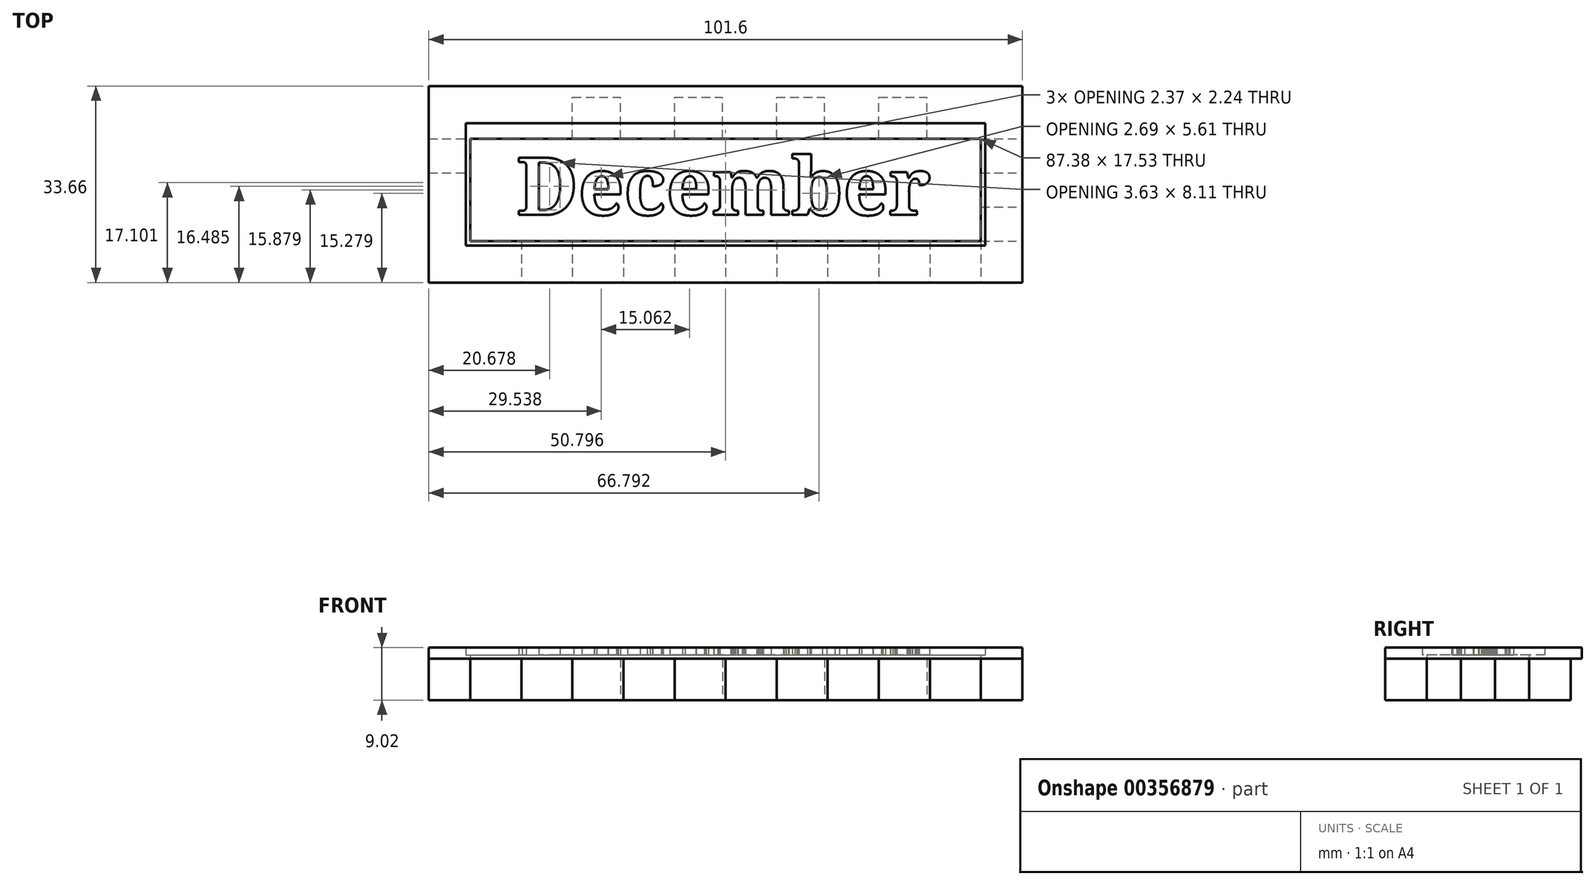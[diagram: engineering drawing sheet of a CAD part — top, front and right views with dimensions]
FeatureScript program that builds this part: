
annotation { "Feature Type Name" : "Feature", "Feature Type Description" : "" }
export const myFeature = defineFeature(function(context is Context, id is Id, definition is map)
    precondition{}
    {
        {
            var Q0;
            Q0=qCreatedBy(makeId("Top.planeOp"),FACE);
            var sketch = newSketch(context, id + "F0", { "sketchPlane" : qUnion([Q0])});
            skLineSegment(sketch, "E0.bottom", {"start": v(-52.12, 11.37) * mm, "end": v(49.48, 11.37) * mm});
            skLineSegment(sketch, "E0.top", {"start": v(-52.12, -20.38) * mm, "end": v(49.48, -20.38) * mm});
            skLineSegment(sketch, "E0.left", {"start": v(-52.12, 11.37) * mm, "end": v(-52.12, -20.38) * mm});
            skLineSegment(sketch, "E0.right", {"start": v(49.48, 11.37) * mm, "end": v(49.48, -20.38) * mm});
            skLineSegment(sketch, "E1.bottom", {"start": v(-52.12, 11.37) * mm, "end": v(-45.01, 11.37) * mm});
            skLineSegment(sketch, "E1.top", {"start": v(-52.12, 4.26) * mm, "end": v(-45.01, 4.26) * mm});
            skLineSegment(sketch, "E1.left", {"start": v(-52.12, 11.37) * mm, "end": v(-52.12, 4.26) * mm});
            skLineSegment(sketch, "E1.right", {"start": v(-45.01, 11.37) * mm, "end": v(-45.01, 4.26) * mm});
            skLineSegment(sketch, "E2.bottom", {"start": v(-45.01, 11.37) * mm, "end": v(-36.78, 11.37) * mm});
            skLineSegment(sketch, "E2.top", {"start": v(-45.01, 4.26) * mm, "end": v(-36.78, 4.26) * mm});
            skLineSegment(sketch, "E2.right", {"start": v(-36.78, 11.37) * mm, "end": v(-36.78, 4.26) * mm});
            skLineSegment(sketch, "E3.bottom", {"start": v(-36.78, 4.26) * mm, "end": v(-27.54, 4.26) * mm});
            skLineSegment(sketch, "E3.top", {"start": v(-36.78, 11.37) * mm, "end": v(-27.54, 11.37) * mm});
            skLineSegment(sketch, "E3.left", {"start": v(-36.78, 4.26) * mm, "end": v(-36.78, 11.37) * mm});
            skLineSegment(sketch, "E3.right", {"start": v(-27.54, 4.26) * mm, "end": v(-27.54, 11.37) * mm});
            skLineSegment(sketch, "E4.bottom", {"start": v(-27.54, 4.26) * mm, "end": v(-19.3, 4.26) * mm});
            skLineSegment(sketch, "E4.top", {"start": v(-27.54, 11.37) * mm, "end": v(-19.3, 11.37) * mm});
            skLineSegment(sketch, "E4.right", {"start": v(-19.3, 4.26) * mm, "end": v(-19.3, 11.37) * mm});
            skLineSegment(sketch, "E5.bottom", {"start": v(-19.3, 4.26) * mm, "end": v(-10.06, 4.26) * mm});
            skLineSegment(sketch, "E5.top", {"start": v(-19.3, 11.37) * mm, "end": v(-10.06, 11.37) * mm});
            skLineSegment(sketch, "E5.right", {"start": v(-10.06, 4.26) * mm, "end": v(-10.06, 11.37) * mm});
            skLineSegment(sketch, "E6.bottom", {"start": v(-10.06, 4.26) * mm, "end": v(-10.06, 4.26) * mm});
            skLineSegment(sketch, "E6.top", {"start": v(-10.06, 11.37) * mm, "end": v(-10.06, 11.37) * mm});
            skLineSegment(sketch, "E7.bottom", {"start": v(-10.06, 4.26) * mm, "end": v(-1.83, 4.26) * mm});
            skLineSegment(sketch, "E7.top", {"start": v(-10.06, 11.37) * mm, "end": v(-1.83, 11.37) * mm});
            skLineSegment(sketch, "E7.right", {"start": v(-1.83, 4.26) * mm, "end": v(-1.83, 11.37) * mm});
            skLineSegment(sketch, "E8.bottom", {"start": v(-1.83, 4.26) * mm, "end": v(7.41, 4.26) * mm});
            skLineSegment(sketch, "E8.top", {"start": v(-1.83, 11.37) * mm, "end": v(7.41, 11.37) * mm});
            skLineSegment(sketch, "E8.right", {"start": v(7.41, 4.26) * mm, "end": v(7.41, 11.37) * mm});
            skLineSegment(sketch, "E9.bottom", {"start": v(7.41, 4.26) * mm, "end": v(15.64, 4.26) * mm});
            skLineSegment(sketch, "E9.top", {"start": v(7.41, 11.37) * mm, "end": v(15.64, 11.37) * mm});
            skLineSegment(sketch, "E9.right", {"start": v(15.64, 4.26) * mm, "end": v(15.64, 11.37) * mm});
            skLineSegment(sketch, "E10.bottom", {"start": v(15.64, 4.26) * mm, "end": v(24.89, 4.26) * mm});
            skLineSegment(sketch, "E10.top", {"start": v(15.64, 11.37) * mm, "end": v(24.89, 11.37) * mm});
            skLineSegment(sketch, "E10.right", {"start": v(24.89, 4.26) * mm, "end": v(24.89, 11.37) * mm});
            skLineSegment(sketch, "E11.bottom", {"start": v(24.89, 4.26) * mm, "end": v(24.89, 4.26) * mm});
            skLineSegment(sketch, "E11.top", {"start": v(24.89, 11.37) * mm, "end": v(24.89, 11.37) * mm});
            skLineSegment(sketch, "E12.bottom", {"start": v(24.89, 4.26) * mm, "end": v(33.12, 4.26) * mm});
            skLineSegment(sketch, "E12.top", {"start": v(24.89, 11.37) * mm, "end": v(33.12, 11.37) * mm});
            skLineSegment(sketch, "E12.right", {"start": v(33.12, 4.26) * mm, "end": v(33.12, 11.37) * mm});
            skLineSegment(sketch, "E13.bottom", {"start": v(33.12, 4.26) * mm, "end": v(42.36, 4.26) * mm});
            skLineSegment(sketch, "E13.top", {"start": v(33.12, 11.37) * mm, "end": v(42.36, 11.37) * mm});
            skLineSegment(sketch, "E13.right", {"start": v(42.36, 4.26) * mm, "end": v(42.36, 11.37) * mm});
            skLineSegment(sketch, "E14.bottom", {"start": v(42.36, 4.26) * mm, "end": v(49.48, 4.26) * mm});
            skLineSegment(sketch, "E14.top", {"start": v(42.36, 11.37) * mm, "end": v(49.48, 11.37) * mm});
            skLineSegment(sketch, "E14.right", {"start": v(49.48, 4.26) * mm, "end": v(49.48, 11.37) * mm});
            skLineSegment(sketch, "E15.bottom", {"start": v(-52.12, -20.38) * mm, "end": v(-45.01, -20.38) * mm});
            skLineSegment(sketch, "E15.top", {"start": v(-52.12, -13.26) * mm, "end": v(-45.01, -13.26) * mm});
            skLineSegment(sketch, "E15.left", {"start": v(-52.12, -20.38) * mm, "end": v(-52.12, -13.26) * mm});
            skLineSegment(sketch, "E15.right", {"start": v(-45.01, -20.38) * mm, "end": v(-45.01, -13.26) * mm});
            skLineSegment(sketch, "E16.bottom", {"start": v(-45.01, -13.26) * mm, "end": v(-45.01, -13.26) * mm});
            skLineSegment(sketch, "E16.top", {"start": v(-45.01, -20.38) * mm, "end": v(-45.01, -20.38) * mm});
            skLineSegment(sketch, "E16.left", {"start": v(-45.01, -13.26) * mm, "end": v(-45.01, -20.38) * mm});
            skLineSegment(sketch, "E16.right", {"start": v(-45.01, -13.26) * mm, "end": v(-45.01, -20.38) * mm});
            skLineSegment(sketch, "E17.bottom", {"start": v(-45.01, -13.26) * mm, "end": v(-36.27, -13.26) * mm});
            skLineSegment(sketch, "E17.top", {"start": v(-45.01, -20.38) * mm, "end": v(-36.27, -20.38) * mm});
            skLineSegment(sketch, "E17.right", {"start": v(-36.27, -13.26) * mm, "end": v(-36.27, -20.38) * mm});
            skLineSegment(sketch, "E18.bottom", {"start": v(-36.27, -13.26) * mm, "end": v(-36.27, -13.26) * mm});
            skLineSegment(sketch, "E18.top", {"start": v(-36.27, -20.38) * mm, "end": v(-36.27, -20.38) * mm});
            skLineSegment(sketch, "E19.bottom", {"start": v(-36.27, -13.26) * mm, "end": v(-27.54, -13.26) * mm});
            skLineSegment(sketch, "E19.top", {"start": v(-36.27, -20.38) * mm, "end": v(-27.54, -20.38) * mm});
            skLineSegment(sketch, "E19.right", {"start": v(-27.54, -13.26) * mm, "end": v(-27.54, -20.38) * mm});
            skLineSegment(sketch, "E20.bottom", {"start": v(-27.54, -13.26) * mm, "end": v(-18.8, -13.26) * mm});
            skLineSegment(sketch, "E20.top", {"start": v(-27.54, -20.38) * mm, "end": v(-18.8, -20.38) * mm});
            skLineSegment(sketch, "E20.right", {"start": v(-18.8, -13.26) * mm, "end": v(-18.8, -20.38) * mm});
            skLineSegment(sketch, "E21.bottom", {"start": v(-18.8, -13.26) * mm, "end": v(-10.06, -13.26) * mm});
            skLineSegment(sketch, "E21.top", {"start": v(-18.8, -20.38) * mm, "end": v(-10.06, -20.38) * mm});
            skLineSegment(sketch, "E21.right", {"start": v(-10.06, -13.26) * mm, "end": v(-10.06, -20.38) * mm});
            skLineSegment(sketch, "E22.bottom", {"start": v(-10.06, -13.26) * mm, "end": v(-1.32, -13.26) * mm});
            skLineSegment(sketch, "E22.top", {"start": v(-10.06, -20.38) * mm, "end": v(-1.32, -20.38) * mm});
            skLineSegment(sketch, "E22.right", {"start": v(-1.32, -13.26) * mm, "end": v(-1.32, -20.38) * mm});
            skLineSegment(sketch, "E23.bottom", {"start": v(-1.32, -13.26) * mm, "end": v(7.41, -13.26) * mm});
            skLineSegment(sketch, "E23.top", {"start": v(-1.32, -20.38) * mm, "end": v(7.41, -20.38) * mm});
            skLineSegment(sketch, "E23.right", {"start": v(7.41, -13.26) * mm, "end": v(7.41, -20.38) * mm});
            skLineSegment(sketch, "E24.bottom", {"start": v(7.41, -13.26) * mm, "end": v(16.15, -13.26) * mm});
            skLineSegment(sketch, "E24.top", {"start": v(7.41, -20.38) * mm, "end": v(16.15, -20.38) * mm});
            skLineSegment(sketch, "E24.right", {"start": v(16.15, -13.26) * mm, "end": v(16.15, -20.38) * mm});
            skLineSegment(sketch, "E25.bottom", {"start": v(16.15, -13.26) * mm, "end": v(24.89, -13.26) * mm});
            skLineSegment(sketch, "E25.top", {"start": v(16.15, -20.38) * mm, "end": v(24.89, -20.38) * mm});
            skLineSegment(sketch, "E25.right", {"start": v(24.89, -13.26) * mm, "end": v(24.89, -20.38) * mm});
            skLineSegment(sketch, "E26.bottom", {"start": v(24.89, -13.26) * mm, "end": v(33.63, -13.26) * mm});
            skLineSegment(sketch, "E26.top", {"start": v(24.89, -20.38) * mm, "end": v(33.63, -20.38) * mm});
            skLineSegment(sketch, "E26.right", {"start": v(33.63, -13.26) * mm, "end": v(33.63, -20.38) * mm});
            skLineSegment(sketch, "E27.bottom", {"start": v(33.63, -13.26) * mm, "end": v(42.36, -13.26) * mm});
            skLineSegment(sketch, "E27.top", {"start": v(33.63, -20.38) * mm, "end": v(42.36, -20.38) * mm});
            skLineSegment(sketch, "E27.right", {"start": v(42.36, -13.26) * mm, "end": v(42.36, -20.38) * mm});
            skLineSegment(sketch, "E28.bottom", {"start": v(42.36, -13.26) * mm, "end": v(49.48, -13.26) * mm});
            skLineSegment(sketch, "E28.top", {"start": v(42.36, -20.38) * mm, "end": v(49.48, -20.38) * mm});
            skLineSegment(sketch, "E28.right", {"start": v(49.48, -13.26) * mm, "end": v(49.48, -20.38) * mm});
            skLineSegment(sketch, "E29.top", {"start": v(-52.12, -1.58) * mm, "end": v(-45.01, -1.58) * mm});
            skLineSegment(sketch, "E29.left", {"start": v(-52.12, 4.26) * mm, "end": v(-52.12, -1.58) * mm});
            skLineSegment(sketch, "E29.right", {"start": v(-45.01, 4.26) * mm, "end": v(-45.01, -1.58) * mm});
            skLineSegment(sketch, "E30.top", {"start": v(-52.12, -7.42) * mm, "end": v(-45.01, -7.42) * mm});
            skLineSegment(sketch, "E30.left", {"start": v(-52.12, -1.58) * mm, "end": v(-52.12, -7.42) * mm});
            skLineSegment(sketch, "E30.right", {"start": v(-45.01, -1.58) * mm, "end": v(-45.01, -7.42) * mm});
            skLineSegment(sketch, "E31.bottom", {"start": v(-45.01, -7.42) * mm, "end": v(-52.12, -7.42) * mm});
            skLineSegment(sketch, "E31.top", {"start": v(-45.01, -13.26) * mm, "end": v(-52.12, -13.26) * mm});
            skLineSegment(sketch, "E31.left", {"start": v(-45.01, -7.42) * mm, "end": v(-45.01, -13.26) * mm});
            skLineSegment(sketch, "E31.right", {"start": v(-52.12, -7.42) * mm, "end": v(-52.12, -13.26) * mm});
            skLineSegment(sketch, "E32.top", {"start": v(42.36, -1.58) * mm, "end": v(49.48, -1.58) * mm});
            skLineSegment(sketch, "E32.left", {"start": v(42.36, 4.26) * mm, "end": v(42.36, -1.58) * mm});
            skLineSegment(sketch, "E32.right", {"start": v(49.48, 4.26) * mm, "end": v(49.48, -1.58) * mm});
            skLineSegment(sketch, "E33.top", {"start": v(42.36, -7.42) * mm, "end": v(49.48, -7.42) * mm});
            skLineSegment(sketch, "E33.left", {"start": v(42.36, -1.58) * mm, "end": v(42.36, -7.42) * mm});
            skLineSegment(sketch, "E33.right", {"start": v(49.48, -1.58) * mm, "end": v(49.48, -7.42) * mm});
            skLineSegment(sketch, "E34.left", {"start": v(42.36, -7.42) * mm, "end": v(42.36, -13.26) * mm});
            skLineSegment(sketch, "E34.right", {"start": v(49.48, -7.42) * mm, "end": v(49.48, -13.26) * mm});
            skSolve(sketch);
        }
        {
            var Q0;
            Q0=makeQuery(id+"F0.imprint","IMPRINT",FACE,{"disambiguationData":[TD([[makeQuery(id+"F0.imprint","IMPRINT",EDGE,{"derivedFrom":sQuery(id+"F0.wireOp",EDGE,"E2.top")}),-1.0]])]});
            var Q1;
            Q1=makeQuery(id+"F0.imprint","IMPRINT",FACE,{"disambiguationData":[TD([[makeQuery(id+"F0.imprint","IMPRINT",EDGE,{"derivedFrom":sQuery(id+"F0.wireOp",EDGE,"E2.bottom")}),-1.0]])]});
            var Q2;
            Q2=makeQuery(id+"F0.imprint","IMPRINT",FACE,{"disambiguationData":[TD([[makeQuery(id+"F0.imprint","IMPRINT",EDGE,{"derivedFrom":sQuery(id+"F0.wireOp",EDGE,"E4.bottom")}),1.0]])]});
            var Q3;
            Q3=makeQuery(id+"F0.imprint","IMPRINT",FACE,{"disambiguationData":[TD([[makeQuery(id+"F0.imprint","IMPRINT",EDGE,{"derivedFrom":sQuery(id+"F0.wireOp",EDGE,"E7.bottom")}),1.0]])]});
            var Q4;
            Q4=makeQuery(id+"F0.imprint","IMPRINT",FACE,{"disambiguationData":[TD([[makeQuery(id+"F0.imprint","IMPRINT",EDGE,{"derivedFrom":sQuery(id+"F0.wireOp",EDGE,"E9.bottom")}),1.0]])]});
            var Q5;
            Q5=makeQuery(id+"F0.imprint","IMPRINT",FACE,{"disambiguationData":[TD([[makeQuery(id+"F0.imprint","IMPRINT",EDGE,{"derivedFrom":sQuery(id+"F0.wireOp",EDGE,"E12.bottom")}),1.0]])]});
            var Q6;
            Q6=makeQuery(id+"F0.imprint","IMPRINT",FACE,{"disambiguationData":[TD([[makeQuery(id+"F0.imprint","IMPRINT",EDGE,{"derivedFrom":sQuery(id+"F0.wireOp",EDGE,"E14.bottom")}),-1.0]])]});
            var Q7;
            Q7=makeQuery(id+"F0.imprint","IMPRINT",FACE,{"disambiguationData":[TD([[makeQuery(id+"F0.imprint","IMPRINT",EDGE,{"derivedFrom":sQuery(id+"F0.wireOp",EDGE,"E33.top")}),-1.0]])]});
            var Q8;
            Q8=makeQuery(id+"F0.imprint","IMPRINT",FACE,{"disambiguationData":[TD([[makeQuery(id+"F0.imprint","IMPRINT",EDGE,{"derivedFrom":sQuery(id+"F0.wireOp",EDGE,"E27.bottom")}),-1.0]])]});
            var Q9;
            Q9=makeQuery(id+"F0.imprint","IMPRINT",FACE,{"disambiguationData":[TD([[makeQuery(id+"F0.imprint","IMPRINT",EDGE,{"derivedFrom":sQuery(id+"F0.wireOp",EDGE,"E25.bottom")}),-1.0]])]});
            var Q10;
            Q10=makeQuery(id+"F0.imprint","IMPRINT",FACE,{"disambiguationData":[TD([[makeQuery(id+"F0.imprint","IMPRINT",EDGE,{"derivedFrom":sQuery(id+"F0.wireOp",EDGE,"E23.bottom")}),-1.0]])]});
            var Q11;
            Q11=makeQuery(id+"F0.imprint","IMPRINT",FACE,{"disambiguationData":[TD([[makeQuery(id+"F0.imprint","IMPRINT",EDGE,{"derivedFrom":sQuery(id+"F0.wireOp",EDGE,"E21.bottom")}),-1.0]])]});
            var Q12;
            Q12=makeQuery(id+"F0.imprint","IMPRINT",FACE,{"disambiguationData":[TD([[makeQuery(id+"F0.imprint","IMPRINT",EDGE,{"derivedFrom":sQuery(id+"F0.wireOp",EDGE,"E19.bottom")}),-1.0]])]});
            var Q13;
            Q13=makeQuery(id+"F0.imprint","IMPRINT",FACE,{"disambiguationData":[TD([[makeQuery(id+"F0.imprint","IMPRINT",EDGE,{"derivedFrom":sQuery(id+"F0.wireOp",EDGE,"E31.bottom")}),1.0]])]});
            var Q14;
            Q14=makeQuery(id+"F0.imprint","IMPRINT",FACE,{"disambiguationData":[TD([[makeQuery(id+"F0.imprint","IMPRINT",EDGE,{"derivedFrom":sQuery(id+"F0.wireOp",EDGE,"E1.top")}),-1.0]])]});
            extrude(context, id + "F1", {"entities" : qUnion([Q0, Q1, Q2, Q3, Q4, Q5, Q6, Q7, Q8, Q9, Q10, Q11, Q12, Q13, Q14]), "depth" : 7.11 * mm});
        }
        {
            var Q0;
            Q0=makeQuery(id+"F1.opExtrude","CAP_FACE",FACE,{"disambiguationData":[OSD([sQuery(id+"F0.wireOp",EDGE,"E2.bottom"),sQuery(id+"F0.wireOp",EDGE,"E1.right"),sQuery(id+"F0.wireOp",EDGE,"E3.bottom"),sQuery(id+"F0.wireOp",EDGE,"E3.left"),sQuery(id+"F0.wireOp",EDGE,"E4.top"),sQuery(id+"F0.wireOp",EDGE,"E3.right"),sQuery(id+"F0.wireOp",EDGE,"E5.bottom"),sQuery(id+"F0.wireOp",EDGE,"E4.right"),sQuery(id+"F0.wireOp",EDGE,"E6.top"),sQuery(id+"F0.wireOp",EDGE,"E5.right"),sQuery(id+"F0.wireOp",EDGE,"E7.bottom"),sQuery(id+"F0.wireOp",EDGE,"E5.right"),sQuery(id+"F0.wireOp",EDGE,"E8.top"),sQuery(id+"F0.wireOp",EDGE,"E7.right"),sQuery(id+"F0.wireOp",EDGE,"E9.bottom"),sQuery(id+"F0.wireOp",EDGE,"E8.right"),sQuery(id+"F0.wireOp",EDGE,"E10.top"),sQuery(id+"F0.wireOp",EDGE,"E9.right"),sQuery(id+"F0.wireOp",EDGE,"E11.bottom"),sQuery(id+"F0.wireOp",EDGE,"E10.right"),sQuery(id+"F0.wireOp",EDGE,"E12.top"),sQuery(id+"F0.wireOp",EDGE,"E10.right"),sQuery(id+"F0.wireOp",EDGE,"E13.bottom"),sQuery(id+"F0.wireOp",EDGE,"E12.right"),sQuery(id+"F0.wireOp",EDGE,"E16.bottom"),sQuery(id+"F0.wireOp",EDGE,"E17.top"),sQuery(id+"F0.wireOp",EDGE,"E16.left"),sQuery(id+"F0.wireOp",EDGE,"E18.bottom"),sQuery(id+"F0.wireOp",EDGE,"E17.right"),sQuery(id+"F0.wireOp",EDGE,"E19.top"),sQuery(id+"F0.wireOp",EDGE,"E17.right"),sQuery(id+"F0.wireOp",EDGE,"E20.bottom"),sQuery(id+"F0.wireOp",EDGE,"E19.right"),sQuery(id+"F0.wireOp",EDGE,"E21.top"),sQuery(id+"F0.wireOp",EDGE,"E20.right"),sQuery(id+"F0.wireOp",EDGE,"E22.bottom"),sQuery(id+"F0.wireOp",EDGE,"E21.right"),sQuery(id+"F0.wireOp",EDGE,"E23.top"),sQuery(id+"F0.wireOp",EDGE,"E22.right"),sQuery(id+"F0.wireOp",EDGE,"E24.bottom"),sQuery(id+"F0.wireOp",EDGE,"E23.right"),sQuery(id+"F0.wireOp",EDGE,"E25.top"),sQuery(id+"F0.wireOp",EDGE,"E24.right"),sQuery(id+"F0.wireOp",EDGE,"E26.bottom"),sQuery(id+"F0.wireOp",EDGE,"E25.right"),sQuery(id+"F0.wireOp",EDGE,"E27.top"),sQuery(id+"F0.wireOp",EDGE,"E26.right"),sQuery(id+"F0.wireOp",EDGE,"E27.right"),sQuery(id+"F0.wireOp",EDGE,"E1.top"),sQuery(id+"F0.wireOp",EDGE,"E29.left"),sQuery(id+"F0.wireOp",EDGE,"E29.top"),sQuery(id+"F0.wireOp",EDGE,"E30.right"),sQuery(id+"F0.wireOp",EDGE,"E31.bottom"),sQuery(id+"F0.wireOp",EDGE,"E31.top"),sQuery(id+"F0.wireOp",EDGE,"E31.right"),sQuery(id+"F0.wireOp",EDGE,"E14.bottom"),sQuery(id+"F0.wireOp",EDGE,"E32.right"),sQuery(id+"F0.wireOp",EDGE,"E32.top"),sQuery(id+"F0.wireOp",EDGE,"E33.left"),sQuery(id+"F0.wireOp",EDGE,"E33.top"),sQuery(id+"F0.wireOp",EDGE,"E28.bottom"),sQuery(id+"F0.wireOp",EDGE,"E34.right")])],"isStart":false});
            var sketch = newSketch(context, id + "F2", { "sketchPlane" : qUnion([Q0])});
            skLineSegment(sketch, "E35.bottom", {"start": v(-52.12, -20.38) * mm, "end": v(-45.01, -20.38) * mm});
            skLineSegment(sketch, "E35.top", {"start": v(-52.12, 13.28) * mm, "end": v(-45.01, 13.28) * mm});
            skLineSegment(sketch, "E35.left", {"start": v(-52.12, -20.38) * mm, "end": v(-52.12, 13.28) * mm});
            skLineSegment(sketch, "E35.right", {"start": v(-45.01, -20.38) * mm, "end": v(-45.01, 13.28) * mm});
            skLineSegment(sketch, "E36.bottom", {"start": v(-52.12, -20.38) * mm, "end": v(49.48, -20.38) * mm});
            skLineSegment(sketch, "E36.top", {"start": v(-52.12, -13.26) * mm, "end": v(49.48, -13.26) * mm});
            skLineSegment(sketch, "E36.left", {"start": v(-52.12, -20.38) * mm, "end": v(-52.12, -13.26) * mm});
            skLineSegment(sketch, "E36.right", {"start": v(49.48, -20.38) * mm, "end": v(49.48, -13.26) * mm});
            skPoint(sketch, "E37.oppositeSnap0", {"position": v(42.36, -4.5) * mm});
            skLineSegment(sketch, "E37.bottom", {"start": v(49.48, -20.38) * mm, "end": v(42.36, -20.38) * mm});
            skLineSegment(sketch, "E37.top", {"start": v(49.48, 13.28) * mm, "end": v(42.36, 13.28) * mm});
            skLineSegment(sketch, "E37.left", {"start": v(49.48, -20.38) * mm, "end": v(49.48, 13.28) * mm});
            skLineSegment(sketch, "E37.right", {"start": v(42.36, -20.38) * mm, "end": v(42.36, 13.28) * mm});
            skLineSegment(sketch, "E38.bottom", {"start": v(-52.12, 13.28) * mm, "end": v(49.48, 13.28) * mm});
            skLineSegment(sketch, "E38.top", {"start": v(-52.12, 4.26) * mm, "end": v(49.48, 4.26) * mm});
            skLineSegment(sketch, "E38.left", {"start": v(-52.12, 13.28) * mm, "end": v(-52.12, 4.26) * mm});
            skLineSegment(sketch, "E38.right", {"start": v(49.48, 13.28) * mm, "end": v(49.48, 4.26) * mm});
            skSolve(sketch);
        }
        {
            var Q0;
            Q0=qSketchRegion(id+"F2",true);
            var Q1;
            {var subQ5=sQuery(id+"F2.wireOp",EDGE,"E36.top");var subQ10=sQuery(id+"F2.wireOp",EDGE,"E35.right");var subQ12=makeQuery(id+"F2.imprint","INTERSECT",VERTEX,{"derivedFrom":[makeQuery(id+"F1.opExtrude","CAP_EDGE",EDGE,{"disambiguationData":[OSD([sQuery(id+"F0.wireOp",EDGE,"E31.bottom")])],"isStart":false}),subQ10]});var subQ24=makeQuery(id+"F2.imprint","INTERSECT",VERTEX,{"derivedFrom":[subQ10,subQ5]});Q1=makeQuery(id+"F2.imprint","IMPRINT",FACE,{"disambiguationData":[TD([[makeQuery(id+"F2.imprint","IMPRINT",EDGE,{"disambiguationData":[TD([[subQ12,1.0],[subQ24,-1.0]])],"derivedFrom":subQ10}),-1.0]])]});}
            extrude(context, id + "F3", {"entities" : qUnion([Q0, Q1]), "depth" : 0.64 * mm});
        }
        {
            var Q0;
            Q0=makeQuery(id+"F3.opExtrude","CAP_FACE",FACE,{"disambiguationData":[OSD([sQuery(id+"F2.wireOp",EDGE,"E35.left"),sQuery(id+"F2.wireOp",EDGE,"E36.bottom"),sQuery(id+"F2.wireOp",EDGE,"E36.left"),sQuery(id+"F2.wireOp",EDGE,"E37.bottom"),sQuery(id+"F2.wireOp",EDGE,"E37.left"),sQuery(id+"F2.wireOp",EDGE,"E38.bottom"),sQuery(id+"F2.wireOp",EDGE,"E38.left"),sQuery(id+"F2.wireOp",EDGE,"E38.right")])],"isStart":false});
            var sketch = newSketch(context, id + "F4", { "sketchPlane" : qUnion([Q0])});
            skLineSegment(sketch, "E39.bottom", {"start": v(-52.12, 13.28) * mm, "end": v(49.48, 13.28) * mm});
            skLineSegment(sketch, "E39.top", {"start": v(-52.12, 6.93) * mm, "end": v(49.48, 6.93) * mm});
            skLineSegment(sketch, "E39.left", {"start": v(-52.12, 13.28) * mm, "end": v(-52.12, 6.93) * mm});
            skLineSegment(sketch, "E39.right", {"start": v(49.48, 13.28) * mm, "end": v(49.48, 6.93) * mm});
            skLineSegment(sketch, "E40.bottom", {"start": v(-52.12, 13.28) * mm, "end": v(-45.77, 13.28) * mm});
            skLineSegment(sketch, "E40.top", {"start": v(-52.12, -20.38) * mm, "end": v(-45.77, -20.38) * mm});
            skLineSegment(sketch, "E40.left", {"start": v(-52.12, 13.28) * mm, "end": v(-52.12, -20.38) * mm});
            skLineSegment(sketch, "E40.right", {"start": v(-45.77, 13.28) * mm, "end": v(-45.77, -20.38) * mm});
            skLineSegment(sketch, "E41.bottom", {"start": v(-52.12, -14.03) * mm, "end": v(49.48, -14.03) * mm});
            skLineSegment(sketch, "E41.top", {"start": v(-52.12, -20.38) * mm, "end": v(49.48, -20.38) * mm});
            skLineSegment(sketch, "E41.left", {"start": v(-52.12, -14.03) * mm, "end": v(-52.12, -20.38) * mm});
            skLineSegment(sketch, "E41.right", {"start": v(49.48, -14.03) * mm, "end": v(49.48, -20.38) * mm});
            skLineSegment(sketch, "E42.bottom", {"start": v(49.48, -20.38) * mm, "end": v(43.13, -20.38) * mm});
            skLineSegment(sketch, "E42.top", {"start": v(49.48, 13.28) * mm, "end": v(43.13, 13.28) * mm});
            skLineSegment(sketch, "E42.left", {"start": v(49.48, -20.38) * mm, "end": v(49.48, 13.28) * mm});
            skLineSegment(sketch, "E42.right", {"start": v(43.13, -20.38) * mm, "end": v(43.13, 13.28) * mm});
            skSolve(sketch);
        }
        {
            var Q0;
            Q0=qSketchRegion(id+"F4",true);
            extrude(context, id + "F5", {"entities" : qUnion([Q0]), "operationType" : NewBodyOperationType.ADD, "depth" : 1.27 * mm});
        }
        {
            var Q0;
            Q0=makeQuery(id+"F3.opExtrude","CAP_FACE",FACE,{"disambiguationData":[OSD([sQuery(id+"F2.wireOp",EDGE,"E35.left"),sQuery(id+"F2.wireOp",EDGE,"E36.bottom"),sQuery(id+"F2.wireOp",EDGE,"E36.left"),sQuery(id+"F2.wireOp",EDGE,"E37.bottom"),sQuery(id+"F2.wireOp",EDGE,"E37.left"),sQuery(id+"F2.wireOp",EDGE,"E38.bottom"),sQuery(id+"F2.wireOp",EDGE,"E38.left"),sQuery(id+"F2.wireOp",EDGE,"E38.right")])],"isStart":false});
            var sketch = newSketch(context, id + "F6", { "sketchPlane" : qUnion([Q0])});
            skText(sketch, "E43", { "text": "December", "fontName": "NotoSerif-Bold.ttf"});
            const initialGuessF6  = {"E43": [-0.03708, -0.0088, 1, 0, 0.00988]};
            skSetInitialGuess(sketch, initialGuessF6);
            skSolve(sketch);
        }
        {
            var Q0;
            Q0 = qSketchRegion(id + "F6", true);
            extrude(context, id + "F7", {"entities" : qUnion([Q0]), "operationType" : NewBodyOperationType.ADD, "depth" : 1.27 * mm});
        }
    });
